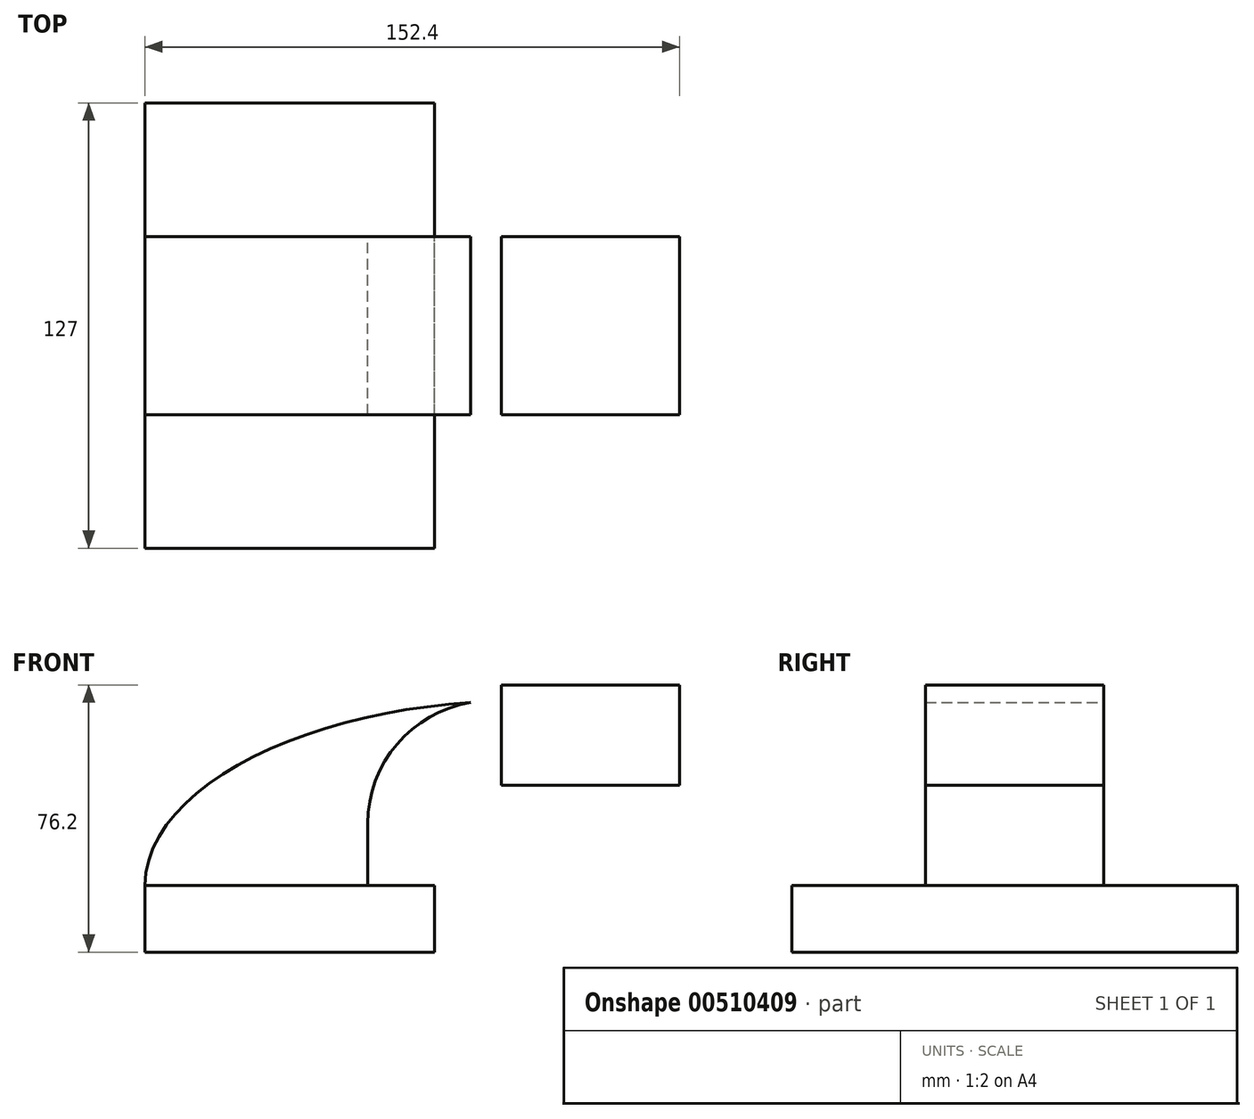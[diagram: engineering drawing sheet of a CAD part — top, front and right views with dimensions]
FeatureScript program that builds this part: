
annotation { "Feature Type Name" : "Feature", "Feature Type Description" : "" }
export const myFeature = defineFeature(function(context is Context, id is Id, definition is map)
    precondition{}
    {
        {
            var Q0;
            Q0=qCreatedBy(makeId("Front.planeOp"),FACE);
            var sketch = newSketch(context, id + "F0", { "sketchPlane" : qUnion([Q0])});
            skLineSegment(sketch, "E0.bottom", {"start": v(-41.27, -9.53) * mm, "end": v(41.28, -9.53) * mm});
            skLineSegment(sketch, "E0.top", {"start": v(-41.28, 9.53) * mm, "end": v(41.28, 9.53) * mm});
            skLineSegment(sketch, "E0.left", {"start": v(-41.28, -9.53) * mm, "end": v(-41.28, 9.53) * mm});
            skLineSegment(sketch, "E0.right", {"start": v(41.28, -9.53) * mm, "end": v(41.28, 9.52) * mm});
            skPoint(sketch, "E0.middle", {"position": v(0, 0) * mm});
            skLineSegment(sketch, "E1.bottom", {"start": v(111.12, 38.1) * mm, "end": v(60.32, 38.1) * mm});
            skLineSegment(sketch, "E1.top", {"start": v(111.12, 66.68) * mm, "end": v(60.32, 66.68) * mm});
            skLineSegment(sketch, "E1.left", {"start": v(111.13, 38.1) * mm, "end": v(111.13, 66.68) * mm});
            skLineSegment(sketch, "E1.right", {"start": v(60.33, 38.1) * mm, "end": v(60.33, 66.68) * mm});
            skPoint(sketch, "E1.middle", {"position": v(85.72, 52.39) * mm});
            skLineSegment(sketch, "E2", {"start": v(41.28, 9.52) * mm, "end": v(41.28, 27.13) * mm});
            skArc(sketch, "E3", {"start": v(41.27, 27.13) * mm, "mid": v(46.68, 39.06) * mm, "end": v(59.2, 42.88) * mm});
            skLineSegment(sketch, "E4", {"start": v(59.2, 42.88) * mm, "end": v(85.72, 42.88) * mm});
            skPoint(sketch, "E4.endSnap0", {"position": v(85.72, 38.1) * mm});
            skLineSegment(sketch, "E5.0", {"start": v(60.2, 61.93) * mm, "end": v(85.72, 61.93) * mm});
            skArc(sketch, "E5.1", {"start": v(22.22, 27.13) * mm, "mid": v(33.56, 52.89) * mm, "end": v(60.2, 61.93) * mm});
            skLineSegment(sketch, "E5.2", {"start": v(22.22, 9.52) * mm, "end": v(22.22, 27.13) * mm});
            skLineSegment(sketch, "E6", {"start": v(85.72, 38.1) * mm, "end": v(85.72, 66.68) * mm});
            skFitSpline(sketch, "E7", {"points": [v(-41.27, 9.53) * mm, v(60.2, 61.93) * mm], "startDerivative": vector(1.27, 88.91) * mm, "endDerivative": vector(152.97, 1.94) * mm});
            skSolve(sketch);
        }
        {
            var Q0;
            Q0=makeQuery(id+"F0.imprint","IMPRINT",FACE,{"disambiguationData":[TD([[makeQuery(id+"F0.imprint","IMPRINT",EDGE,{"derivedFrom":sQuery(id+"F0.wireOp",EDGE,"E0.bottom")}),1.0]])]});
            extrude(context, id + "F1", {"entities" : qUnion([Q0]), "endBound" : BoundingType.SYMMETRIC, "depth" : 127 * mm});
        }
        {
            var Q0;
            {var subQ0=sQuery(id+"F0.wireOp",EDGE,"E7");var subQ1=sQuery(id+"F0.wireOp",EDGE,"E5.1");var subQ3=makeQuery(id+"F0.imprint","INTERSECT",VERTEX,{"derivedFrom":[subQ1,subQ0]});Q0=makeQuery(id+"F0.imprint","IMPRINT",FACE,{"disambiguationData":[TD([[makeQuery(id+"F0.imprint","IMPRINT",EDGE,{"disambiguationData":[TD([[subQ3,-1.0]])],"derivedFrom":subQ1}),-1.0]])]});}
            var Q1;
            Q1=makeQuery(id+"F0.imprint","IMPRINT",FACE,{"disambiguationData":[TD([[makeQuery(id+"F0.imprint","IMPRINT",EDGE,{"derivedFrom":sQuery(id+"F0.wireOp",EDGE,"E0.bottom")}),1.0]])]});
            var Q2;
            {var subQ3=sQuery(id+"F0.wireOp",EDGE,"E5.2");Q2=makeQuery(id+"F0.imprint","IMPRINT",FACE,{"disambiguationData":[TD([[makeQuery(id+"F0.imprint","IMPRINT",EDGE,{"derivedFrom":subQ3}),1.0]])]});}
            var Q3;
            {var subQ0=sQuery(id+"F0.wireOp",EDGE,"E1.right");var subQ1=sQuery(id+"F0.wireOp",EDGE,"E1.bottom");var subQ2=makeQuery(id+"F0.imprint","INTERSECT",VERTEX,{"derivedFrom":[subQ1,subQ0]});Q3=makeQuery(id+"F0.imprint","IMPRINT",FACE,{"disambiguationData":[TD([[makeQuery(id+"F0.imprint","IMPRINT",EDGE,{"disambiguationData":[TD([[subQ2,1.0]])],"derivedFrom":subQ1}),-1.0]])]});}
            var Q4;
            {var subQ0=sQuery(id+"F0.wireOp",EDGE,"E1.right");var subQ1=sQuery(id+"F0.wireOp",EDGE,"E1.top");var subQ2=makeQuery(id+"F0.imprint","INTERSECT",VERTEX,{"derivedFrom":[subQ1,subQ0]});Q4=makeQuery(id+"F0.imprint","IMPRINT",FACE,{"disambiguationData":[TD([[makeQuery(id+"F0.imprint","IMPRINT",EDGE,{"disambiguationData":[TD([[subQ2,1.0]])],"derivedFrom":subQ1}),1.0]])]});}
            var Q5;
            {var subQ0=sQuery(id+"F0.wireOp",EDGE,"E1.left");Q5=makeQuery(id+"F0.imprint","IMPRINT",FACE,{"disambiguationData":[TD([[makeQuery(id+"F0.imprint","IMPRINT",EDGE,{"derivedFrom":subQ0}),1.0]])]});}
            var Q6;
            {var subQ0=sQuery(id+"F0.wireOp",EDGE,"E4");var subQ1=sQuery(id+"F0.wireOp",EDGE,"E1.right");var subQ2=makeQuery(id+"F0.imprint","INTERSECT",VERTEX,{"derivedFrom":[subQ1,subQ0]});Q6=makeQuery(id+"F0.imprint","IMPRINT",FACE,{"disambiguationData":[TD([[makeQuery(id+"F0.imprint","IMPRINT",EDGE,{"disambiguationData":[TD([[subQ2,-1.0]])],"derivedFrom":subQ1}),-1.0]])]});}
            extrude(context, id + "F2", {"entities" : qUnion([Q0, Q1, Q2, Q3, Q4, Q5, Q6]), "operationType" : NewBodyOperationType.ADD, "endBound" : BoundingType.SYMMETRIC, "depth" : 50.8 * mm});
        }
    });
